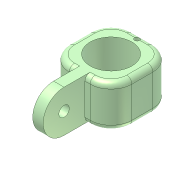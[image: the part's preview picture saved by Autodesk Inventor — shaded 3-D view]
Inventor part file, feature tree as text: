
AUTODESK INVENTOR PART (.ipt)
format: ipt  version: unknown  size: 265,216 bytes
history: native  units: mm
features: extrude x3, fillet x3, sketch x3
ambient origin geometry x8: Origin, YZ Plane, XZ Plane, XY Plane, X Axis, Y Axis, Z Axis, Center Point
feature tree (9):
  extrude  "Extrusion1"  Depth=4.0mm TaperAngle=0.0deg
  fillet  "Fillet2"  Radius=3.0mm
  fillet  "Fillet3"  Radius=1.0mm
  extrude  "Extrusion4"  Depth=2.0mm
  extrude  "Extrusion5"  Depth=1.0mm
  fillet  "Fillet4"  Radius=3.0mm
  sketch  "Sketch1"  dims[d0=4.0mm d7=4.0mm d8=0.0mm d13=3.0mm d14=1.0mm]
  sketch  "Sketch4"  dims[d15=4.0mm d19=2.0mm]
  sketch  "Sketch5"  dims[d20=2.0mm d21=1.0mm d22=3.0mm d23=0.0mm d24=0.5mm d25=10.0mm d26=0.0mm d27=0.5mm]
